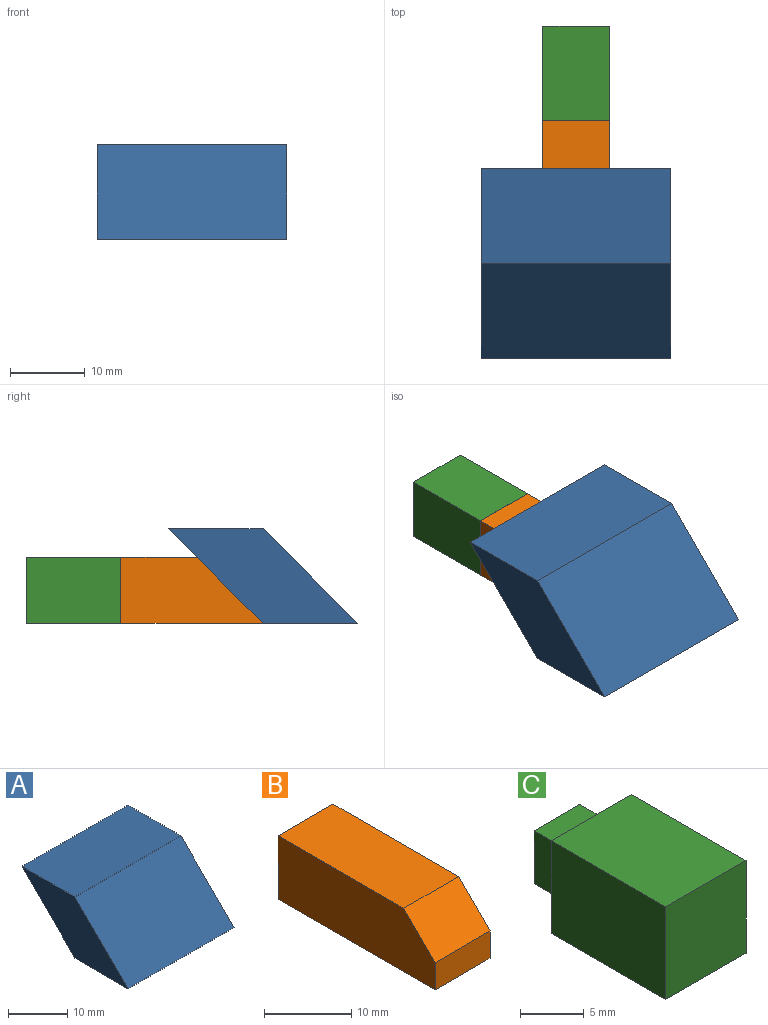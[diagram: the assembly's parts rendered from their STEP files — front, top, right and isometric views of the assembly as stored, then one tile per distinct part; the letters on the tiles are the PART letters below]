
ASSEMBLY  parts=3 mates=2
PART A: 6 faces, bbox 25.4x25.4x12.7 mm
  f0: plane 25.4x12.7mm, normal (0,0,-1), area 322.6mm2, adj f1,f3,f4,f5
  f1: plane 25.4x12.7mm, normal (1,0,0), area 161.3mm2, adj f0,f2,f4,f5
  f2: plane 25.4x12.7mm, normal (0,0,1), area 322.6mm2, adj f1,f3,f4,f5
  f3: plane 25.4x12.7mm, normal (-1,0,0), area 161.3mm2, adj f0,f2,f4,f5
  f4: plane 25.4x12.7mm, normal (0,0.71,-0.71), area 456.2mm2, adj f0,f1,f2,f3
  f5: plane 25.4x12.7mm, normal (0,-0.71,0.71), area 456.2mm2, adj f0,f1,f2,f3
PART B: 12 faces, bbox 8.9x25.4x8.9 mm
  f0: plane 8.89x8.89mm, normal (0,1,0), area 53.2mm2, adj f1,f2,f3,f4,f6,f7,f8,f9
  f1: plane 25.4x8.89mm, normal (-1,0,0), area 212.9mm2, adj f0,f2,f4,f5,f11
  f2: plane 25.4x8.89mm, normal (0,0,-1), area 225.8mm2, adj f0,f1,f3,f5
  f3: plane 25.4x8.89mm, normal (1,0,0), area 212.9mm2, adj f0,f2,f4,f5,f11
  f4: plane 20.32x8.89mm, normal (0,0,1), area 180.6mm2, adj f0,f1,f3,f11
  f5: plane 8.89x3.81mm, normal (0,-1,0), area 33.9mm2, adj f1,f2,f3,f11
  f6: plane 5.08x3.81mm, normal (1,0,0), area 19.4mm2, adj f0,f7,f9,f10
  f7: plane 5.08x3.81mm, normal (0,0,1), area 19.4mm2, adj f0,f6,f8,f10
  f8: plane 5.08x3.81mm, normal (-1,0,0), area 19.4mm2, adj f0,f7,f9,f10
  f9: plane 5.08x3.81mm, normal (0,0,-1), area 19.4mm2, adj f0,f6,f8,f10
  f10: plane 5.08x5.08mm, normal (0,1,0), area 25.8mm2, adj f6,f7,f8,f9
  f11: plane 8.89x5.08mm, normal (0,-0.71,0.71), area 63.9mm2, adj f1,f3,f4,f5
PART C: 11 faces, bbox 8.9x16.5x8.9 mm
  f0: plane 5.08x3.81mm, normal (0,0,-1), area 19.4mm2, adj f1,f3,f4,f10
  f1: plane 5.08x3.81mm, normal (1,0,0), area 19.4mm2, adj f0,f2,f4,f10
  f2: plane 5.08x3.81mm, normal (0,0,1), area 19.4mm2, adj f1,f3,f4,f10
  f3: plane 5.08x3.81mm, normal (-1,0,0), area 19.4mm2, adj f0,f2,f4,f10
  f4: plane 5.08x5.08mm, normal (0,1,0), area 25.8mm2, adj f0,f1,f2,f3
  f5: plane 12.7x8.89mm, normal (0,0,-1), area 112.9mm2, adj f6,f8,f9,f10
  f6: plane 12.7x8.89mm, normal (1,0,0), area 112.9mm2, adj f5,f7,f9,f10
  f7: plane 12.7x8.89mm, normal (0,0,1), area 112.9mm2, adj f6,f8,f9,f10
  f8: plane 12.7x8.89mm, normal (-1,0,0), area 112.9mm2, adj f5,f7,f9,f10
  f9: plane 8.89x8.89mm, normal (0,-1,0), area 79mm2, adj f5,f6,f7,f8
  f10: plane 8.89x8.89mm, normal (0,1,0), area 53.2mm2, adj f0,f1,f2,f3,f5,f6,f7,f8
PLACE A t=(-4.84,-22.09,-4.65)mm
PLACE B t=(-4.84,-15.74,-6.56)mm
PLACE C rot(axis=(-1,0,0),180deg) t=(-17.53,-19.55,-0.21)mm
MATE fastened B.f10 <-> C.f4  axis (0,1,0) through (-17.53,-19.55,-0.21)mm
MATE fastened A.f0 <-> B.f2  axis (0,0,-1) through (-17.54,-41.14,-4.65)mm
